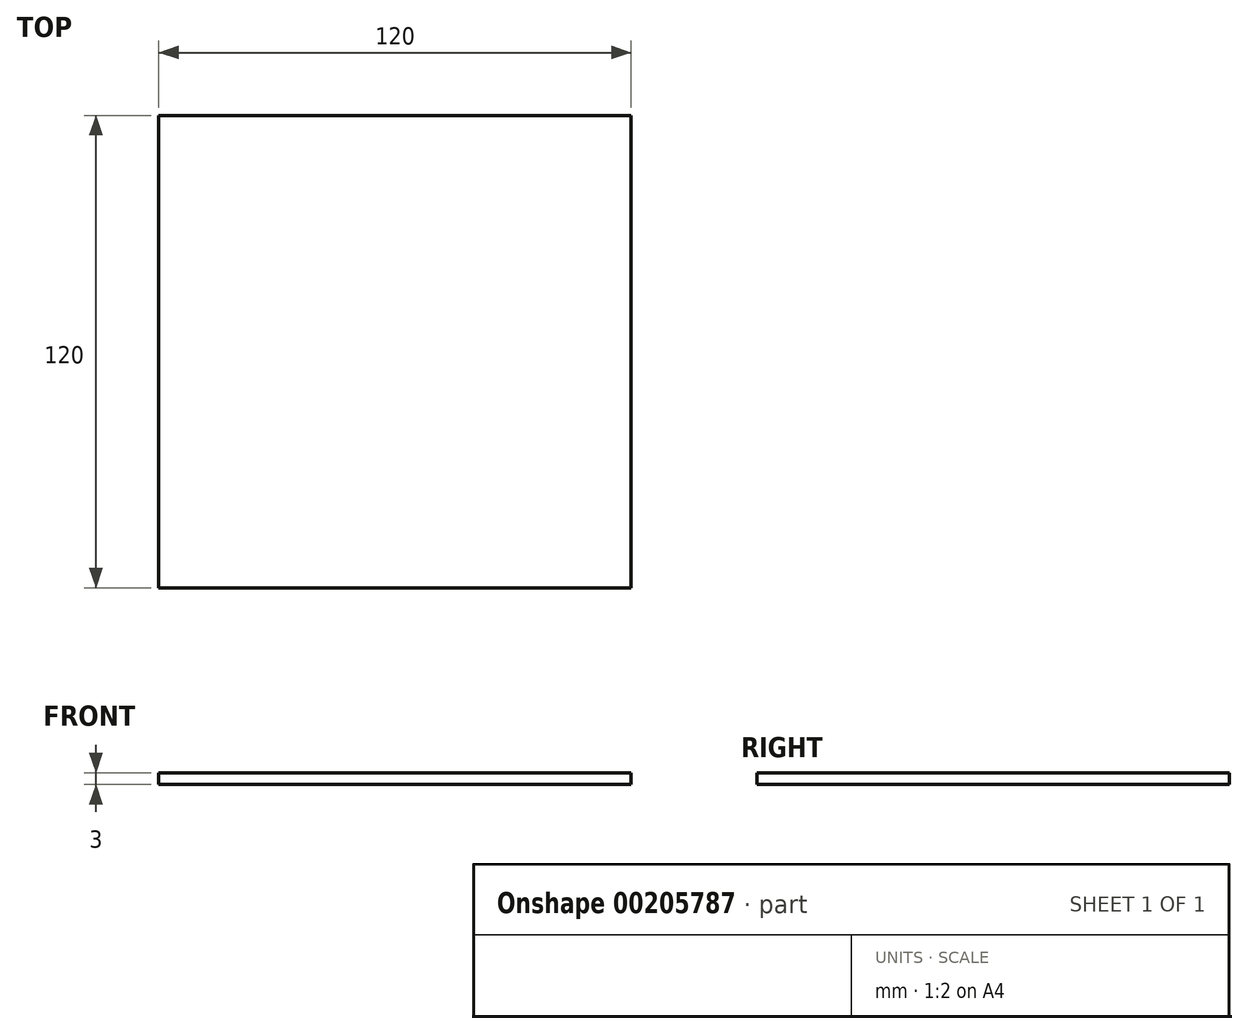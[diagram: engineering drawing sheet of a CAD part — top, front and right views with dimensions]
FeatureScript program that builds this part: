
annotation { "Feature Type Name" : "Feature", "Feature Type Description" : "" }
export const myFeature = defineFeature(function(context is Context, id is Id, definition is map)
    precondition{}
    {
        {
            var Q0;
            Q0=qCreatedBy(makeId("Top.planeOp"),FACE);
            var sketch = newSketch(context, id + "F0", { "sketchPlane" : qUnion([Q0])});
            skLineSegment(sketch, "E0.bottom", {"start": v(-60, -60) * mm, "end": v(60, -60) * mm});
            skLineSegment(sketch, "E0.top", {"start": v(-60, 60) * mm, "end": v(60, 60) * mm});
            skLineSegment(sketch, "E0.left", {"start": v(-60, -60) * mm, "end": v(-60, 60) * mm});
            skLineSegment(sketch, "E0.right", {"start": v(60, -60) * mm, "end": v(60, 60) * mm});
            skPoint(sketch, "E0.middle", {"position": v(0, 0) * mm});
            skSolve(sketch);
        }
        {
            var Q0;
            Q0 = qSketchRegion(id + "F0", true);
            extrude(context, id + "F1", {"entities" : qUnion([Q0]), "oppositeDirection" : true, "depth" : 3 * mm});
        }
    });
